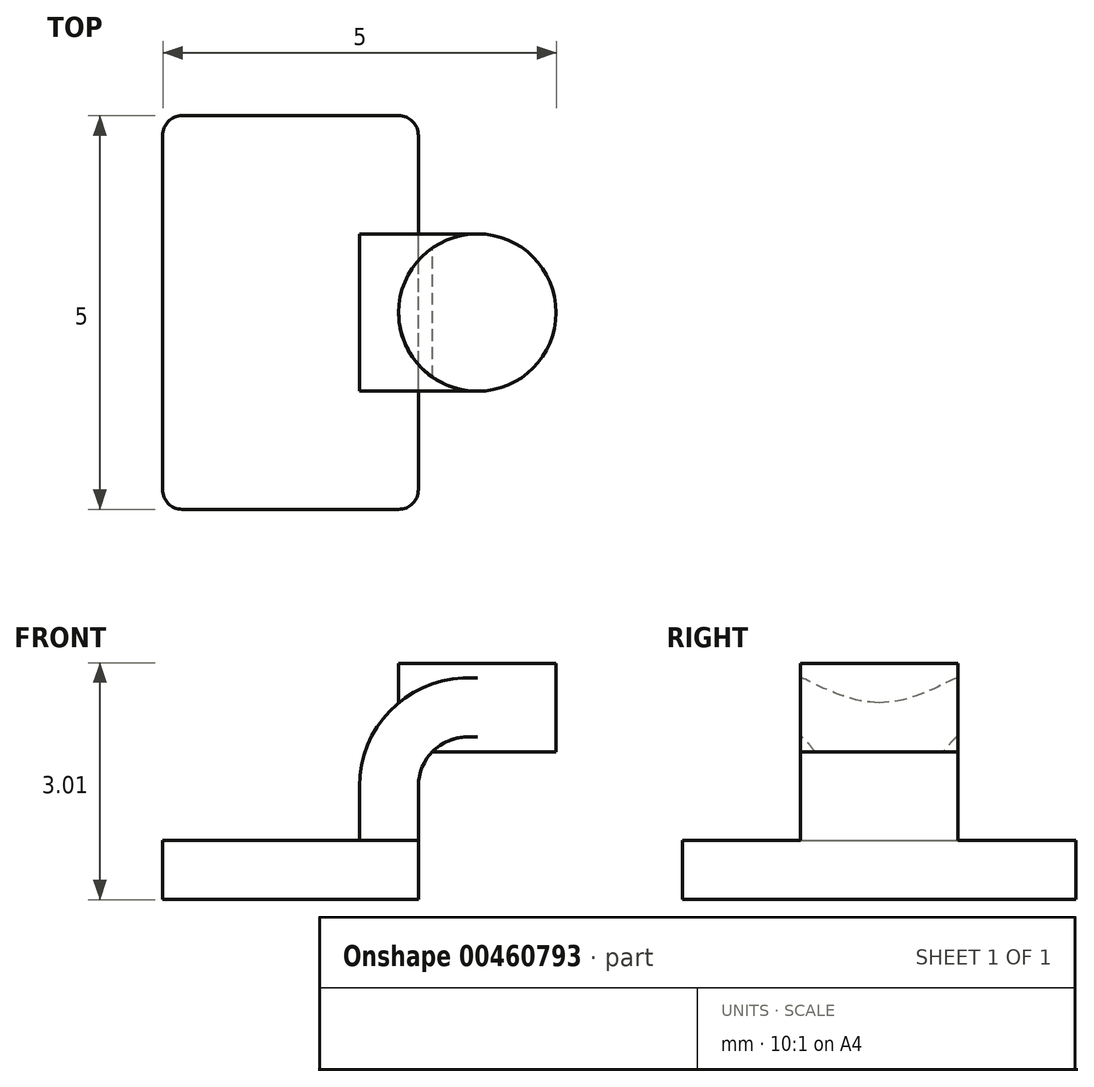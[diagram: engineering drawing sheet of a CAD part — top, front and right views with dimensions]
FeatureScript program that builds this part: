
annotation { "Feature Type Name" : "Feature", "Feature Type Description" : "" }
export const myFeature = defineFeature(function(context is Context, id is Id, definition is map)
    precondition{}
    {
        {
            var Q0;
            Q0=qCreatedBy(makeId("Front.planeOp"),FACE);
            var sketch = newSketch(context, id + "F0", { "sketchPlane" : qUnion([Q0])});
            skLineSegment(sketch, "E0.bottom", {"start": v(1.63, -0.37) * mm, "end": v(-1.62, -0.37) * mm});
            skLineSegment(sketch, "E0.top", {"start": v(1.62, 0.38) * mm, "end": v(-1.62, 0.38) * mm});
            skLineSegment(sketch, "E0.left", {"start": v(1.63, -0.37) * mm, "end": v(1.63, 0.38) * mm});
            skLineSegment(sketch, "E0.right", {"start": v(-1.62, -0.37) * mm, "end": v(-1.62, 0.38) * mm});
            skPoint(sketch, "E0.middle", {"position": v(0, 0) * mm});
            skLineSegment(sketch, "E1.bottom", {"start": v(2.37, 1.5) * mm, "end": v(4.37, 1.5) * mm});
            skLineSegment(sketch, "E1.top", {"start": v(2.37, 2.63) * mm, "end": v(4.37, 2.63) * mm});
            skLineSegment(sketch, "E1.left", {"start": v(2.37, 1.5) * mm, "end": v(2.37, 2.63) * mm});
            skLineSegment(sketch, "E1.right", {"start": v(4.37, 1.5) * mm, "end": v(4.37, 2.63) * mm});
            skPoint(sketch, "E1.middle", {"position": v(3.37, 2.06) * mm});
            skLineSegment(sketch, "E2", {"start": v(1.62, 0.38) * mm, "end": v(1.62, 1.06) * mm});
            skArc(sketch, "E3", {"start": v(1.62, 1.06) * mm, "mid": v(1.8, 1.5) * mm, "end": v(2.25, 1.69) * mm});
            skLineSegment(sketch, "E4", {"start": v(2.25, 1.69) * mm, "end": v(2.37, 1.69) * mm});
            skLineSegment(sketch, "E5.0", {"start": v(2.25, 2.44) * mm, "end": v(2.37, 2.44) * mm});
            skArc(sketch, "E5.1", {"start": v(0.87, 1.06) * mm, "mid": v(1.28, 2.04) * mm, "end": v(2.25, 2.44) * mm});
            skLineSegment(sketch, "E5.2", {"start": v(0.87, 0.38) * mm, "end": v(0.87, 1.06) * mm});
            skFitSpline(sketch, "E6", {"points": [v(2.25, 2.44) * mm, v(-1.62, 0.38) * mm], "startDerivative": vector(-6.75, -0.13) * mm, "endDerivative": vector(-0.06, -5.47) * mm});
            skLineSegment(sketch, "E7", {"start": v(3.37, 2.63) * mm, "end": v(3.37, 1.5) * mm});
            skSolve(sketch);
        }
        {
            var Q0;
            Q0=makeQuery(id+"F0.imprint","IMPRINT",FACE,{"disambiguationData":[TD([[makeQuery(id+"F0.imprint","IMPRINT",EDGE,{"derivedFrom":sQuery(id+"F0.wireOp",EDGE,"E0.bottom")}),-1.0]])]});
            extrude(context, id + "F1", {"entities" : qUnion([Q0]), "endBound" : BoundingType.SYMMETRIC, "depth" : 5 * mm});
        }
        {
            var Q0;
            {var subQ1=sQuery(id+"F0.wireOp",EDGE,"E2");Q0=makeQuery(id+"F0.imprint","IMPRINT",FACE,{"disambiguationData":[TD([[makeQuery(id+"F0.imprint","IMPRINT",EDGE,{"derivedFrom":subQ1}),1.0]])]});}
            extrude(context, id + "F2", {"entities" : qUnion([Q0]), "operationType" : NewBodyOperationType.ADD, "endBound" : BoundingType.SYMMETRIC, "depth" : 2 * mm});
        }
        {
            var Q0;
            {var subQ4=sQuery(id+"F0.wireOp",EDGE,"E5.1");Q0=makeQuery(id+"F0.imprint","IMPRINT",FACE,{"disambiguationData":[TD([[makeQuery(id+"F0.imprint","IMPRINT",EDGE,{"derivedFrom":subQ4}),1.0]])]});}
            extrude(context, id + "F3", {"entities" : qUnion([Q0]), "operationType" : NewBodyOperationType.ADD, "endBound" : BoundingType.SYMMETRIC, "depth" : 0.62 * mm});
        }
        {
            var Q0;
            {var subQ6=sQuery(id+"F0.wireOp",EDGE,"E7");Q0=makeQuery(id+"F0.imprint","IMPRINT",FACE,{"disambiguationData":[TD([[makeQuery(id+"F0.imprint","IMPRINT",EDGE,{"derivedFrom":subQ6}),-1.0]])]});}
            var Q1;
            Q1=sQuery(id+"F0.wireOp",EDGE,"E1.left");
            revolve(context, id + "F4", {"operationType" : NewBodyOperationType.ADD, "entities" : qUnion([Q0]), "axis" : qUnion([Q1]), "revolveType" : RevolveType.FULL});
        }
        {
            var Q0;
            Q0=makeQuery(id+"F1.opExtrude","CAP_EDGE",EDGE,{"disambiguationData":[OSD([sQuery(id+"F0.wireOp",EDGE,"E0.right")])],"isStart":true});
            var Q1;
            Q1=makeQuery(id+"F1.opExtrude","CAP_EDGE",EDGE,{"disambiguationData":[OSD([sQuery(id+"F0.wireOp",EDGE,"E0.left")])],"isStart":true});
            var Q2;
            Q2=makeQuery(id+"F1.opExtrude","CAP_EDGE",EDGE,{"disambiguationData":[OSD([sQuery(id+"F0.wireOp",EDGE,"E0.left")])],"isStart":false});
            var Q3;
            Q3=makeQuery(id+"F1.opExtrude","CAP_EDGE",EDGE,{"disambiguationData":[OSD([sQuery(id+"F0.wireOp",EDGE,"E0.right")])],"isStart":false});
            fillet(context, id + "F5", {"entities" : qUnion([Q0, Q1, Q2, Q3]), "radius" : 0.25 * mm, "tangentPropagation" : true, "allowEdgeOverflow" : false});
        }
    });
